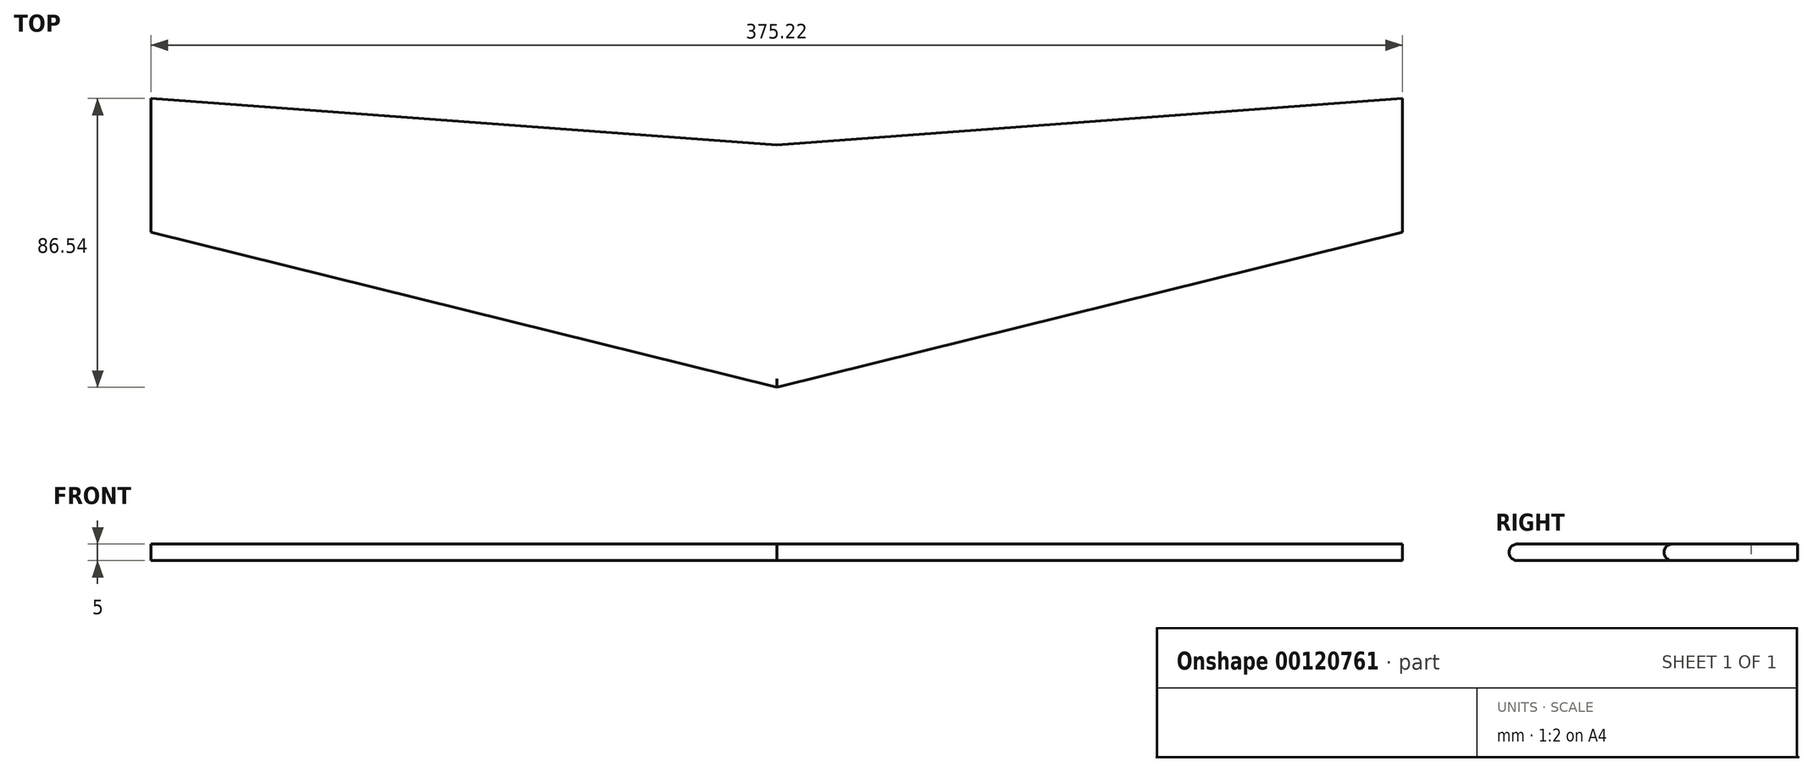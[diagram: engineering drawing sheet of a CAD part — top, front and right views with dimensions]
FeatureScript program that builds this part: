
annotation { "Feature Type Name" : "Feature", "Feature Type Description" : "" }
export const myFeature = defineFeature(function(context is Context, id is Id, definition is map)
    precondition{}
    {
        {
            var Q0;
            Q0=qCreatedBy(makeId("Top.planeOp"),FACE);
            var sketch = newSketch(context, id + "F0", { "sketchPlane" : qUnion([Q0])});
            skLineSegment(sketch, "E0", {"start": v(0, 0) * mm, "end": v(0, 72.57) * mm});
            skLineSegment(sketch, "E1", {"start": v(0, 72.57) * mm, "end": v(0, 72.57) * mm});
            skLineSegment(sketch, "E2", {"start": v(0, 72.57) * mm, "end": v(187.61, 26.1) * mm});
            skLineSegment(sketch, "E3", {"start": v(187.61, -13.97) * mm, "end": v(187.61, 26.1) * mm});
            skLineSegment(sketch, "E4", {"start": v(187.61, -13.97) * mm, "end": v(0, 0) * mm});
            skSolve(sketch);
        }
        {
            var Q0;
            Q0=makeQuery(id+"F0.imprint","IMPRINT",FACE,{"disambiguationData":[TD([[makeQuery(id+"F0.imprint","IMPRINT",EDGE,{"derivedFrom":sQuery(id+"F0.wireOp",EDGE,"E0")}),-1.0]])]});
            extrude(context, id + "F1", {"entities" : qUnion([Q0]), "depth" : 5 * mm});
        }
        {
            var Q0;
            Q0=makeQuery(id+"F1.opExtrude","CAP_EDGE",EDGE,{"disambiguationData":[OSD([sQuery(id+"F0.wireOp",EDGE,"E2")])],"isStart":false});
            fillet(context, id + "F2", {"entities" : qUnion([Q0]), "radius" : 2.5 * mm, "tangentPropagation" : true, "allowEdgeOverflow" : false});
        }
        {
            var Q0;
            Q0=makeQuery(id+"F1.opExtrude","CAP_EDGE",EDGE,{"disambiguationData":[OSD([sQuery(id+"F0.wireOp",EDGE,"E2")])],"isStart":true});
            fillet(context, id + "F3", {"entities" : qUnion([Q0]), "radius" : 2.5 * mm, "tangentPropagation" : true, "allowEdgeOverflow" : false});
        }
        {
            var Q0;
            Q0=makeQuery(id+"F1.opExtrude","SWEPT_BODY",BODY,{"disambiguationData":[OSD([sQuery(id+"F0.wireOp",EDGE,"E0"),sQuery(id+"F0.wireOp",EDGE,"E2"),sQuery(id+"F0.wireOp",EDGE,"E3"),sQuery(id+"F0.wireOp",EDGE,"E4")])]});
            var Q1;
            Q1=qCreatedBy(makeId("Right.planeOp"),FACE);
            mirror(context, id + "F4", {"entities" : qUnion([Q0]), "mirrorPlane" : qUnion([Q1])});
        }
        {
            var Q0;
            Q0=makeQuery(id+"F1.opExtrude","SWEPT_BODY",BODY,{"disambiguationData":[OSD([sQuery(id+"F0.wireOp",EDGE,"E0"),sQuery(id+"F0.wireOp",EDGE,"E2"),sQuery(id+"F0.wireOp",EDGE,"E3"),sQuery(id+"F0.wireOp",EDGE,"E4")])]});
            var Q1;
            Q1=qCreatedBy(makeId("Right.planeOp"),FACE);
            mirror(context, id + "F5", {"operationType" : NewBodyOperationType.ADD, "entities" : qUnion([Q0]), "mirrorPlane" : qUnion([Q1])});
        }
        {
            var Q0;
            Q0=qCreatedBy(makeId("Right.planeOp"),FACE);
            var sketch = newSketch(context, id + "F6", { "sketchPlane" : qUnion([Q0])});
            skLineSegment(sketch, "E5", {"start": v(0, 0) * mm, "end": v(0, 124.51) * mm, "construction": true});
            skSolve(sketch);
        }
        {
            var Q0;
            Q0=makeQuery(id+"F4.opPattern","COPY",BODY,{"derivedFrom":makeQuery(id+"F1.opExtrude","SWEPT_BODY",BODY,{"disambiguationData":[OSD([sQuery(id+"F0.wireOp",EDGE,"E0"),sQuery(id+"F0.wireOp",EDGE,"E2"),sQuery(id+"F0.wireOp",EDGE,"E3"),sQuery(id+"F0.wireOp",EDGE,"E4")])]}),"instanceName":"1"});
            var Q1;
            Q1=sQuery(id+"F6.wireOp",EDGE,"E5");
            transform(context, id + "F7", {"entities" : qUnion([Q0]), "transformType" : TransformType.ROTATION, "transformAxis" : qUnion([Q1]), "angle" : 180 * degree, "makeCopy" : false});
        }
    });
